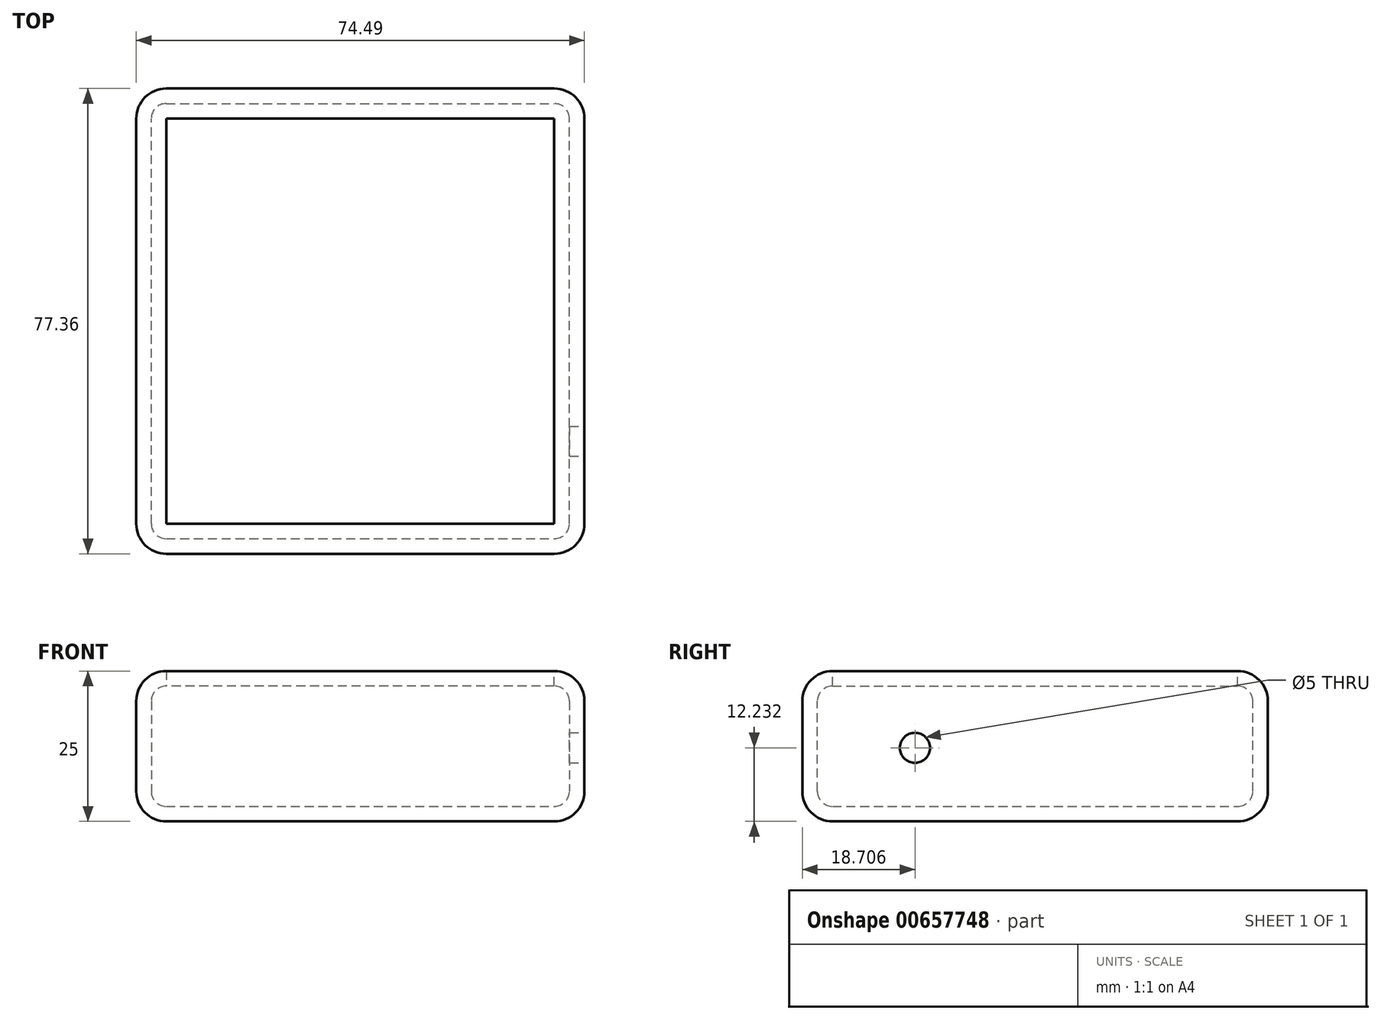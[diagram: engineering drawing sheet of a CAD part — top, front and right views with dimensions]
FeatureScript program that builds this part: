
annotation { "Feature Type Name" : "Feature", "Feature Type Description" : "" }
export const myFeature = defineFeature(function(context is Context, id is Id, definition is map)
    precondition{}
    {
        {
            var Q0;
            Q0=qCreatedBy(makeId("Top.planeOp"),FACE);
            var sketch = newSketch(context, id + "F0", { "sketchPlane" : qUnion([Q0])});
            skLineSegment(sketch, "E0.bottom", {"start": v(-45.18, 37.2) * mm, "end": v(29.31, 37.2) * mm});
            skLineSegment(sketch, "E0.top", {"start": v(-45.18, -40.15) * mm, "end": v(29.31, -40.15) * mm});
            skLineSegment(sketch, "E0.left", {"start": v(-45.18, 37.2) * mm, "end": v(-45.18, -40.15) * mm});
            skLineSegment(sketch, "E0.right", {"start": v(29.31, 37.2) * mm, "end": v(29.31, -40.15) * mm});
            skSolve(sketch);
        }
        {
            var Q0;
            Q0=makeQuery(id+"F0.imprint","IMPRINT",FACE,{"disambiguationData":[TD([[makeQuery(id+"F0.imprint","IMPRINT",EDGE,{"derivedFrom":sQuery(id+"F0.wireOp",EDGE,"E0.bottom")}),-1.0]])]});
            extrude(context, id + "F1", {"entities" : qUnion([Q0]), "depth" : 25 * mm, "offsetDistance" : 25 * mm});
        }
        {
            var Q0;
            Q0=makeQuery(id+"F1.opExtrude","SWEPT_EDGE",EDGE,{"disambiguationData":[OSD([sQuery(id+"F0.wireOp",EDGE,"E0.top"),sQuery(id+"F0.wireOp",EDGE,"E0.right")])]});
            var Q1;
            Q1=makeQuery(id+"F1.opExtrude","CAP_EDGE",EDGE,{"disambiguationData":[OSD([sQuery(id+"F0.wireOp",EDGE,"E0.right")])],"isStart":false});
            var Q2;
            Q2=makeQuery(id+"F1.opExtrude","CAP_EDGE",EDGE,{"disambiguationData":[OSD([sQuery(id+"F0.wireOp",EDGE,"E0.top")])],"isStart":false});
            var Q3;
            Q3=makeQuery(id+"F1.opExtrude","CAP_EDGE",EDGE,{"disambiguationData":[OSD([sQuery(id+"F0.wireOp",EDGE,"E0.left")])],"isStart":false});
            var Q4;
            Q4=makeQuery(id+"F1.opExtrude","CAP_EDGE",EDGE,{"disambiguationData":[OSD([sQuery(id+"F0.wireOp",EDGE,"E0.bottom")])],"isStart":false});
            var Q5;
            Q5=makeQuery(id+"F1.opExtrude","CAP_EDGE",EDGE,{"disambiguationData":[OSD([sQuery(id+"F0.wireOp",EDGE,"E0.right")])],"isStart":true});
            var Q6;
            Q6=makeQuery(id+"F1.opExtrude","CAP_EDGE",EDGE,{"disambiguationData":[OSD([sQuery(id+"F0.wireOp",EDGE,"E0.top")])],"isStart":true});
            var Q7;
            Q7=makeQuery(id+"F1.opExtrude","SWEPT_EDGE",EDGE,{"disambiguationData":[OSD([sQuery(id+"F0.wireOp",EDGE,"E0.bottom"),sQuery(id+"F0.wireOp",EDGE,"E0.right")])]});
            var Q8;
            Q8=makeQuery(id+"F1.opExtrude","SWEPT_EDGE",EDGE,{"disambiguationData":[OSD([sQuery(id+"F0.wireOp",EDGE,"E0.top"),sQuery(id+"F0.wireOp",EDGE,"E0.left")])]});
            var Q9;
            Q9=makeQuery(id+"F1.opExtrude","SWEPT_EDGE",EDGE,{"disambiguationData":[OSD([sQuery(id+"F0.wireOp",EDGE,"E0.bottom"),sQuery(id+"F0.wireOp",EDGE,"E0.left")])]});
            var Q10;
            Q10=makeQuery(id+"F1.opExtrude","CAP_EDGE",EDGE,{"disambiguationData":[OSD([sQuery(id+"F0.wireOp",EDGE,"E0.left")])],"isStart":true});
            var Q11;
            Q11=makeQuery(id+"F1.opExtrude","CAP_EDGE",EDGE,{"disambiguationData":[OSD([sQuery(id+"F0.wireOp",EDGE,"E0.bottom")])],"isStart":true});
            fillet(context, id + "F2", {"entities" : qUnion([Q0, Q1, Q2, Q3, Q4, Q5, Q6, Q7, Q8, Q9, Q10, Q11]), "radius" : 5 * mm, "tangentPropagation" : true, "allowEdgeOverflow" : false});
        }
        {
            var Q0;
            Q0=makeQuery(id+"F1.opExtrude","CAP_FACE",FACE,{"disambiguationData":[OSD([sQuery(id+"F0.wireOp",EDGE,"E0.bottom"),sQuery(id+"F0.wireOp",EDGE,"E0.top"),sQuery(id+"F0.wireOp",EDGE,"E0.left"),sQuery(id+"F0.wireOp",EDGE,"E0.right")])],"isStart":false});
            shell(context, id + "F3", {"entities" : qUnion([Q0]), "thickness" : 2.5 * mm});
        }
        {
            var Q0;
            Q0=makeQuery(id+"F1.opExtrude","SWEPT_FACE",FACE,{"disambiguationData":[OSD([sQuery(id+"F0.wireOp",EDGE,"E0.right")])]});
            var sketch = newSketch(context, id + "F4", { "sketchPlane" : qUnion([Q0])});
            skPoint(sketch, "E1", {"position": v(-21.44, 12.23) * mm});
            skSolve(sketch);
        }
        {
            var Q0;
            Q0=sQuery(id+"F4.wireOp",VERTEX,"E1");
            var Q1;
            Q1=makeQuery(id+"F1.opExtrude","SWEPT_BODY",BODY,{"disambiguationData":[OSD([sQuery(id+"F0.wireOp",EDGE,"E0.bottom"),sQuery(id+"F0.wireOp",EDGE,"E0.top"),sQuery(id+"F0.wireOp",EDGE,"E0.left"),sQuery(id+"F0.wireOp",EDGE,"E0.right")])]});
            hole(context, id + "F5", {"style" : HoleStyle.SIMPLE, "endStyle" : HoleEndStyle.BLIND, "holeDiameter" : 5 * mm, "majorDiameter" : 5 * mm, "holeDepth" : 12 * mm, "isTappedThrough" : true, "tappedDepth" : 12 * mm, "tapClearance" : 3, "locations" : qUnion([Q0]), "scope" : qUnion([Q1])});
        }
    });
